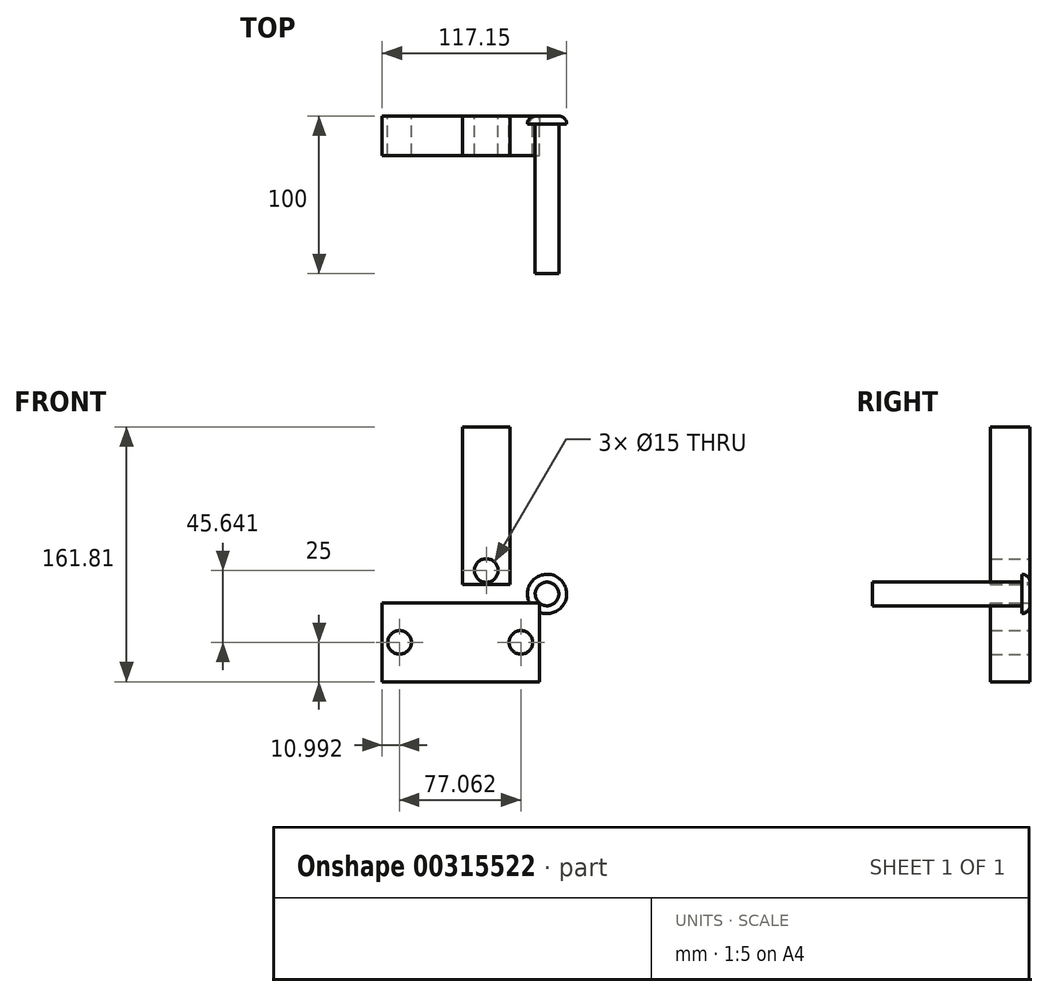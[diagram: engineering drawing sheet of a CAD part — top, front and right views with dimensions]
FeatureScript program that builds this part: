
annotation { "Feature Type Name" : "Feature", "Feature Type Description" : "" }
export const myFeature = defineFeature(function(context is Context, id is Id, definition is map)
    precondition{}
    {
        {
            var Q0;
            Q0=qCreatedBy(makeId("Front.planeOp"),FACE);
            var sketch = newSketch(context, id + "F0", { "sketchPlane" : qUnion([Q0])});
            skLineSegment(sketch, "E0.bottom", {"start": v(-50, -25) * mm, "end": v(50, -25) * mm});
            skLineSegment(sketch, "E0.top", {"start": v(-50, 25) * mm, "end": v(50, 25) * mm});
            skLineSegment(sketch, "E0.left", {"start": v(-50, -25) * mm, "end": v(-50, 25) * mm});
            skLineSegment(sketch, "E0.right", {"start": v(50, -25) * mm, "end": v(50, 25) * mm});
            skPoint(sketch, "E0.middle", {"position": v(38.05, 0) * mm});
            skCircle(sketch, "E1", {"center": v(38.05, 0) * mm, "radius": 7.5 * mm});
            skLineSegment(sketch, "E2", {"start": v(38.05, -25) * mm, "end": v(38.05, 25) * mm, "construction": true});
            skLineSegment(sketch, "E3", {"start": v(38.05, 0) * mm, "end": v(50, 0) * mm, "construction": true});
            skLineSegment(sketch, "E4", {"start": v(-39, 25) * mm, "end": v(-39, -25) * mm, "construction": true});
            skLineSegment(sketch, "E5", {"start": v(-39, -25) * mm, "end": v(-39, 0) * mm, "construction": true});
            skLineSegment(sketch, "E6", {"start": v(-39, 0) * mm, "end": v(-50, 0) * mm, "construction": true});
            skCircle(sketch, "E7", {"center": v(-39, 0) * mm, "radius": 7.5 * mm});
            skSolve(sketch);
        }
        {
            var Q0;
            Q0=makeQuery(id+"F0.imprint","IMPRINT",FACE,{"disambiguationData":[TD([[makeQuery(id+"F0.imprint","IMPRINT",EDGE,{"derivedFrom":sQuery(id+"F0.wireOp",EDGE,"E0.bottom")}),1.0]])]});
            extrude(context, id + "F1", {"entities" : qUnion([Q0]), "depth" : 25 * mm});
        }
        {
            var Q0;
            Q0=qCreatedBy(makeId("Front.planeOp"),FACE);
            var sketch = newSketch(context, id + "F2", { "sketchPlane" : qUnion([Q0])});
            skLineSegment(sketch, "E8.bottom", {"start": v(31.07, 36.8) * mm, "end": v(1.07, 36.8) * mm});
            skLineSegment(sketch, "E8.top", {"start": v(31.07, 136.8) * mm, "end": v(1.07, 136.8) * mm});
            skLineSegment(sketch, "E8.left", {"start": v(31.07, 36.8) * mm, "end": v(31.07, 136.8) * mm});
            skLineSegment(sketch, "E8.right", {"start": v(1.07, 36.8) * mm, "end": v(1.07, 136.8) * mm});
            skPoint(sketch, "E8.middle", {"position": v(16.07, 45.64) * mm});
            skCircle(sketch, "E9", {"center": v(16.07, 45.64) * mm, "radius": 7.5 * mm});
            skLineSegment(sketch, "E10", {"start": v(31.07, 45.64) * mm, "end": v(1.07, 45.64) * mm, "construction": true});
            skLineSegment(sketch, "E11", {"start": v(16.07, 45.64) * mm, "end": v(16.07, 36.8) * mm, "construction": true});
            skSolve(sketch);
        }
        {
            var Q0;
            Q0=makeQuery(id+"F2.imprint","IMPRINT",FACE,{"disambiguationData":[TD([[makeQuery(id+"F2.imprint","IMPRINT",EDGE,{"derivedFrom":sQuery(id+"F2.wireOp",EDGE,"E8.bottom")}),-1.0]])]});
            extrude(context, id + "F3", {"entities" : qUnion([Q0]), "depth" : 25 * mm});
        }
        {
            var Q0;
            Q0=qCreatedBy(makeId("Front.planeOp"),FACE);
            var sketch = newSketch(context, id + "F4", { "sketchPlane" : qUnion([Q0])});
            skCircle(sketch, "E12", {"center": v(54.65, 30.77) * mm, "radius": 7.5 * mm});
            skSolve(sketch);
        }
        {
            var Q0;
            Q0=makeQuery(id+"F4.imprint","IMPRINT",FACE,{"disambiguationData":[TD([[makeQuery(id+"F4.imprint","IMPRINT",EDGE,{"derivedFrom":sQuery(id+"F4.wireOp",EDGE,"E12")}),1.0]])]});
            extrude(context, id + "F5", {"entities" : qUnion([Q0]), "depth" : 100 * mm});
        }
        {
            var Q0;
            Q0=qCreatedBy(makeId("Front.planeOp"),FACE);
            var sketch = newSketch(context, id + "F6", { "sketchPlane" : qUnion([Q0])});
            skCircle(sketch, "E13", {"center": v(54.65, 30.77) * mm, "radius": 12.5 * mm});
            skSolve(sketch);
        }
        {
            var Q0;
            Q0 = qSketchRegion(id + "F6", true);
            extrude(context, id + "F7", {"entities" : qUnion([Q0]), "operationType" : NewBodyOperationType.ADD, "depth" : 5 * mm});
        }
        {
            var Q0;
            Q0=makeQuery(id+"F7.opExtrude","CAP_EDGE",EDGE,{"disambiguationData":[OSD([sQuery(id+"F6.wireOp",EDGE,"E13")])],"isStart":true});
            fillet(context, id + "F8", {"entities" : qUnion([Q0]), "radius" : 5 * mm, "tangentPropagation" : true, "allowEdgeOverflow" : false});
        }
    });
